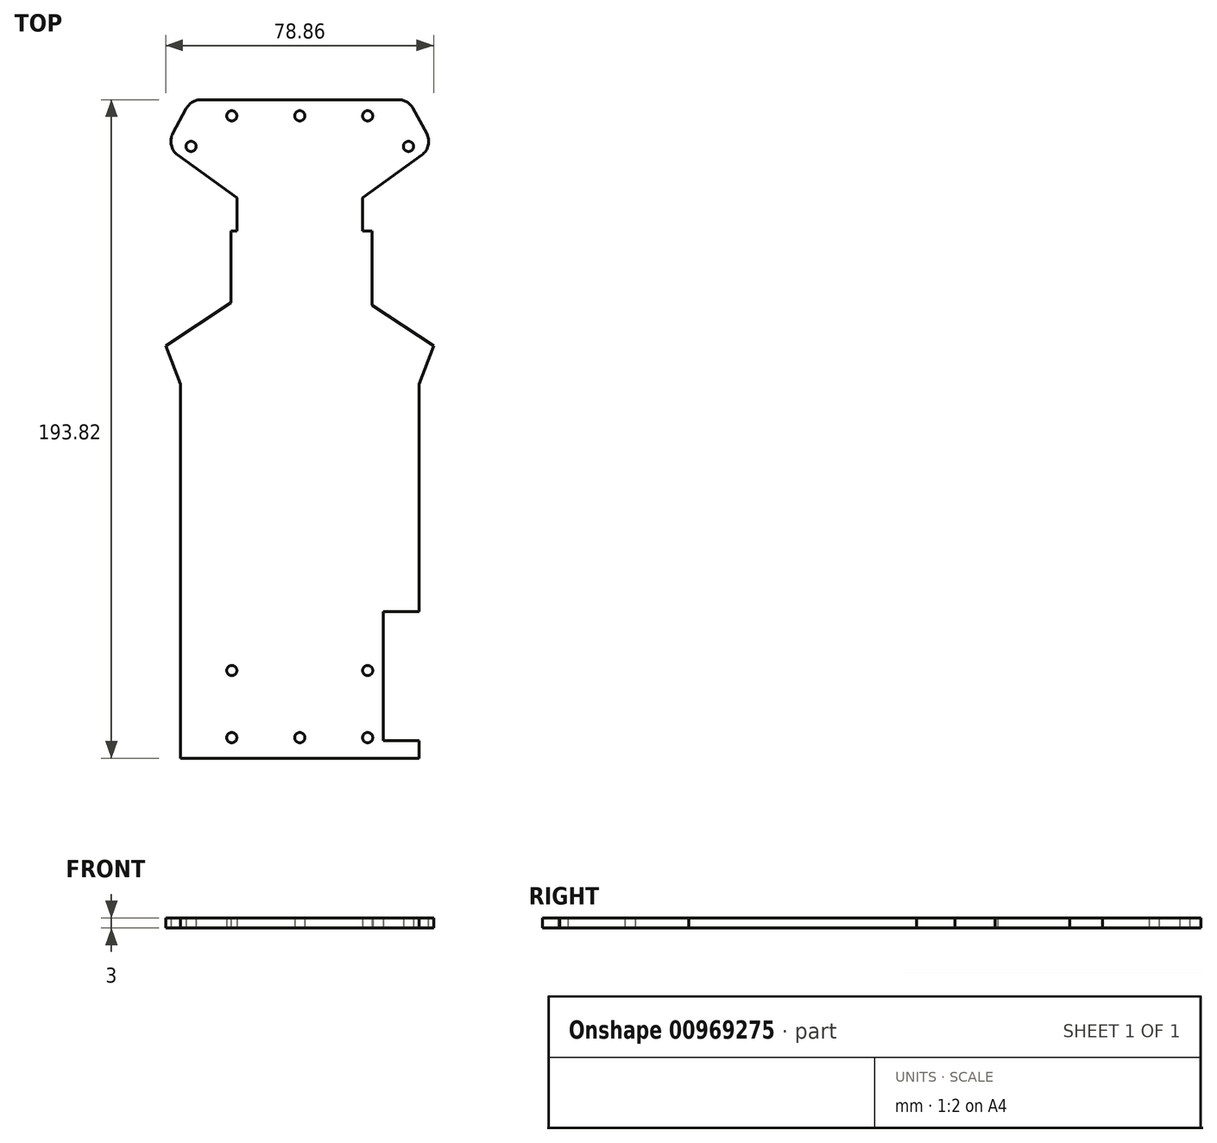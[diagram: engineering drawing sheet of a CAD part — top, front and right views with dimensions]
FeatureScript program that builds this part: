
annotation { "Feature Type Name" : "Feature", "Feature Type Description" : "" }
export const myFeature = defineFeature(function(context is Context, id is Id, definition is map)
    precondition{}
    {
        {
            var Q0;
            Q0=qCreatedBy(makeId("Top.planeOp"),FACE);
            var sketch = newSketch(context, id + "F0", { "sketchPlane" : qUnion([Q0])});
            skCircle(sketch, "E0", {"center": v(0, -88) * mm, "radius": 1.5 * mm});
            skCircle(sketch, "E1", {"center": v(20, -88) * mm, "radius": 1.5 * mm});
            skCircle(sketch, "E2", {"center": v(-20, -88) * mm, "radius": 1.5 * mm});
            skCircle(sketch, "E3", {"center": v(-20, -68.25) * mm, "radius": 1.5 * mm});
            skCircle(sketch, "E4", {"center": v(20, -68.25) * mm, "radius": 1.5 * mm});
            skCircle(sketch, "E5", {"center": v(-20, 95) * mm, "radius": 1.5 * mm});
            skCircle(sketch, "E6", {"center": v(0, 95) * mm, "radius": 1.5 * mm});
            skCircle(sketch, "E7", {"center": v(20, 95) * mm, "radius": 1.5 * mm});
            skCircle(sketch, "E8", {"center": v(-32, 86) * mm, "radius": 1.5 * mm});
            skCircle(sketch, "E9", {"center": v(32, 86) * mm, "radius": 1.5 * mm});
            skLineSegment(sketch, "E10", {"start": v(-20, -88) * mm, "end": v(0, -88) * mm});
            skLineSegment(sketch, "E11", {"start": v(20, -88) * mm, "end": v(0, -88) * mm});
            skLineSegment(sketch, "E12", {"start": v(20, -68.25) * mm, "end": v(20, -88) * mm});
            skLineSegment(sketch, "E13", {"start": v(-20, -88) * mm, "end": v(-20, -68.25) * mm});
            skLineSegment(sketch, "E14", {"start": v(-32, 99.77) * mm, "end": v(32, 99.77) * mm});
            skLineSegment(sketch, "E15", {"start": v(32, 99.77) * mm, "end": v(39.43, 86) * mm});
            skLineSegment(sketch, "E16", {"start": v(-32, 99.77) * mm, "end": v(-39.43, 86) * mm});
            skLineSegment(sketch, "E17", {"start": v(-39.43, 27.36) * mm, "end": v(-35.13, 16.01) * mm});
            skLineSegment(sketch, "E18", {"start": v(-35.13, 16.01) * mm, "end": v(-35.13, -94.05) * mm});
            skLineSegment(sketch, "E19.MirrorCS", {"start": v(39.43, 27.36) * mm, "end": v(35.13, 16.01) * mm});
            skLineSegment(sketch, "E20", {"start": v(-35.13, -94.05) * mm, "end": v(35.13, -94.05) * mm});
            skLineSegment(sketch, "E21", {"start": v(-39.43, 86) * mm, "end": v(-18.49, 70.82) * mm});
            skLineSegment(sketch, "E22", {"start": v(-18.49, 70.82) * mm, "end": v(-18.49, 41.13) * mm});
            skLineSegment(sketch, "E23", {"start": v(-18.49, 41.13) * mm, "end": v(-39.43, 27.36) * mm});
            skLineSegment(sketch, "E24", {"start": v(39.43, 27.36) * mm, "end": v(18.49, 41.13) * mm});
            skLineSegment(sketch, "E25", {"start": v(18.49, 41.13) * mm, "end": v(18.49, 70.82) * mm});
            skLineSegment(sketch, "E26", {"start": v(18.49, 70.82) * mm, "end": v(39.43, 86) * mm});
            skLineSegment(sketch, "E27", {"start": v(35.13, -94.05) * mm, "end": v(35.13, -88.94) * mm});
            skLineSegment(sketch, "E28", {"start": v(35.13, -88.94) * mm, "end": v(24.53, -88.94) * mm});
            skLineSegment(sketch, "E29", {"start": v(24.53, -88.94) * mm, "end": v(24.53, -50.92) * mm});
            skLineSegment(sketch, "E30", {"start": v(24.53, -50.92) * mm, "end": v(35.13, -50.92) * mm});
            skLineSegment(sketch, "E31", {"start": v(35.13, -50.92) * mm, "end": v(35.13, 16.01) * mm});
            skSolve(sketch);
        }
        {
            var Q0;
            Q0=makeQuery(id+"F0.imprint","IMPRINT",FACE,{"disambiguationData":[TD([[makeQuery(id+"F0.imprint","IMPRINT",EDGE,{"derivedFrom":sQuery(id+"F0.wireOp",EDGE,"E3")}),-1.0]])]});
            extrude(context, id + "F1", {"entities" : qUnion([Q0]), "depth" : 3 * mm, "offsetDistance" : 25 * mm});
        }
        {
            var Q0;
            Q0=qCreatedBy(makeId("Top.planeOp"),FACE);
            var sketch = newSketch(context, id + "F2", { "sketchPlane" : qUnion([Q0])});
            skLineSegment(sketch, "E32.bottom", {"start": v(-20.2, -62.6) * mm, "end": v(21.34, -62.6) * mm});
            skLineSegment(sketch, "E32.top", {"start": v(-20.2, 61.14) * mm, "end": v(21.34, 61.14) * mm});
            skLineSegment(sketch, "E32.left", {"start": v(-20.2, -62.6) * mm, "end": v(-20.2, 61.14) * mm});
            skLineSegment(sketch, "E32.right", {"start": v(21.34, -62.6) * mm, "end": v(21.34, 61.14) * mm});
            skSolve(sketch);
        }
        {
            var Q0;
            Q0=makeQuery(id+"F2.imprint","IMPRINT",FACE,{"disambiguationData":[TD([[makeQuery(id+"F2.imprint","IMPRINT",EDGE,{"derivedFrom":sQuery(id+"F2.wireOp",EDGE,"E32.bottom")}),1.0]])]});
            extrude(context, id + "F3", {"entities" : qUnion([Q0]), "operationType" : NewBodyOperationType.ADD, "depth" : 3 * mm, "offsetDistance" : 25 * mm});
        }
        {
            var Q0;
            Q0=makeQuery(id+"F1.opExtrude","SWEPT_EDGE",EDGE,{"disambiguationData":[OSD([sQuery(id+"F0.wireOp",EDGE,"E15"),sQuery(id+"F0.wireOp",EDGE,"E26")])]});
            var Q1;
            Q1=makeQuery(id+"F1.opExtrude","SWEPT_EDGE",EDGE,{"disambiguationData":[OSD([sQuery(id+"F0.wireOp",EDGE,"E14"),sQuery(id+"F0.wireOp",EDGE,"E15")])]});
            var Q2;
            Q2=makeQuery(id+"F1.opExtrude","SWEPT_EDGE",EDGE,{"disambiguationData":[OSD([sQuery(id+"F0.wireOp",EDGE,"E14"),sQuery(id+"F0.wireOp",EDGE,"E16")])]});
            var Q3;
            Q3=makeQuery(id+"F1.opExtrude","SWEPT_EDGE",EDGE,{"disambiguationData":[OSD([sQuery(id+"F0.wireOp",EDGE,"E16"),sQuery(id+"F0.wireOp",EDGE,"E21")])]});
            fillet(context, id + "F4", {"entities" : qUnion([Q0, Q1, Q2, Q3]), "radius" : 5 * mm, "tangentPropagation" : true, "allowEdgeOverflow" : false});
        }
    });
